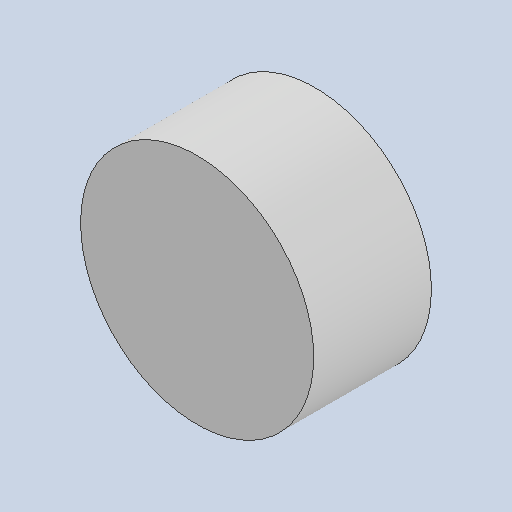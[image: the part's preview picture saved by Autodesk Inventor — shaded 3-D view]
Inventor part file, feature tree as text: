
AUTODESK INVENTOR PART (.ipt)
format: ipt  version: 2022 (Build 260153070, 153G)  size: 104,960 bytes
history: native  units: mm
features: reference x4, other x3, sketch x1, plane x1, extrude x1
ambient origin geometry x8: Origin, YZ Plane, XZ Plane, XY Plane, X Axis, Y Axis, Z Axis, Center Point
bodies: Solid1 (feature_tree)
feature tree (10):
  sketch  "Sketch1"  dims[d0=2.0mm d6=0.15mm d7=0.15mm d8=10.0mm d9=0.0mm]
  plane  "Work Plane1"
  extrude  "Extrusion1"  Depth=10.0mm
  reference  "Reference1"
  reference  "Reference2"
  reference  "Reference3"
  reference  "Reference4"
  other  "<userpath> laptop\Desktop\SumoBot\sumobotENCODER\MotorEncoderAssembly.iam"
  other  "MotorEncoderAssembly.iam"
  other  "TT motor output:1"
